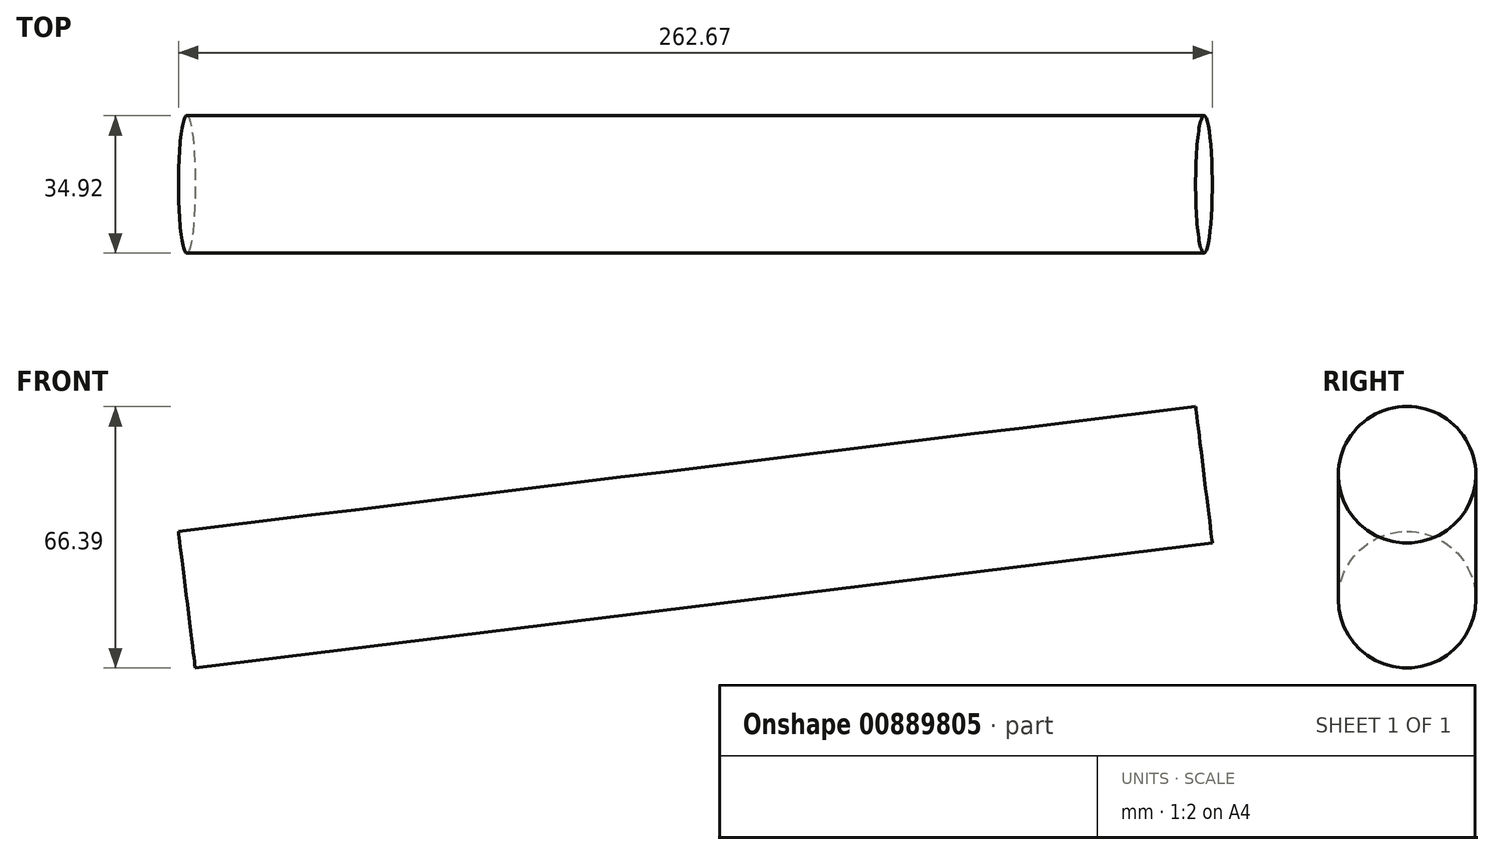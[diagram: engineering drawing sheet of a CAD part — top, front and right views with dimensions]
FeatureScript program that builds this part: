
annotation { "Feature Type Name" : "Feature", "Feature Type Description" : "" }
export const myFeature = defineFeature(function(context is Context, id is Id, definition is map)
    precondition{}
    {
        {
            var Q0;
            Q0=qCreatedBy(makeId("Right.planeOp"),FACE);
            var sketch = newSketch(context, id + "F0", { "sketchPlane" : qUnion([Q0])});
            skLineSegment(sketch, "E0", {"start": v(0, 0) * mm, "end": v(-508, 0) * mm, "construction": true});
            skSolve(sketch);
        }
        {
            var Q0;
            Q0=sQuery(id+"F0.wireOp",EDGE,"E0");
            var Q1;
            Q1=qCreatedBy(makeId("Right.planeOp"),FACE);
            cPlane(context, id + "F1", {"entities" : qUnion([Q0, Q1]), "cplaneType" : CPlaneType.LINE_ANGLE, "offset" : 25.4 * mm, "angle" : 7 * degree, "width" : 152.4 * mm, "height" : 152.4 * mm});
        }
        {
            var Q0;
            Q0=qCreatedBy(id+"F1.planeOp",FACE);
            var sketch = newSketch(context, id + "F2", { "sketchPlane" : qUnion([Q0])});
            skLineSegment(sketch, "E1", {"start": v(0, 0) * mm, "end": v(266.7, 0) * mm, "construction": true});
            skCircle(sketch, "E2", {"center": v(266.7, 0) * mm, "radius": 17.46 * mm});
            skSolve(sketch);
        }
        {
            var Q0;
            Q0=makeQuery(id+"F2.imprint","IMPRINT",FACE,{"disambiguationData":[TD([[makeQuery(id+"F2.imprint","IMPRINT",EDGE,{"derivedFrom":sQuery(id+"F2.wireOp",EDGE,"E2")}),1.0]])]});
            extrude(context, id + "F3", {"entities" : qUnion([Q0]), "oppositeDirection" : true, "depth" : 260.35 * mm, "offsetDistance" : 25.4 * mm});
        }
    });
